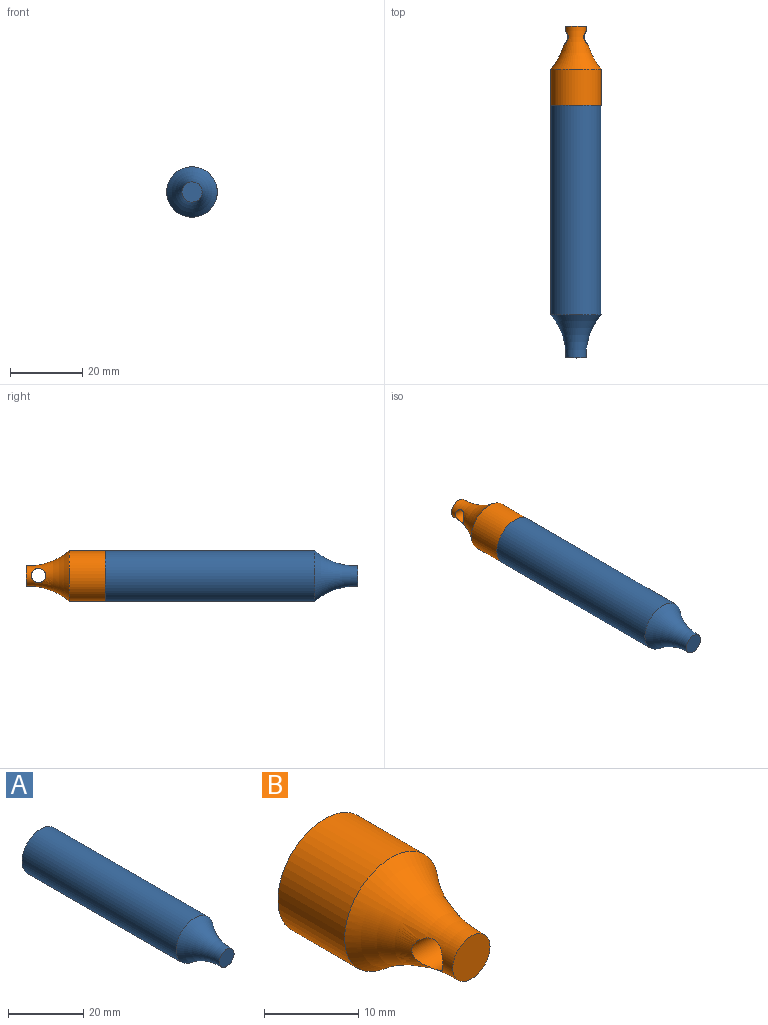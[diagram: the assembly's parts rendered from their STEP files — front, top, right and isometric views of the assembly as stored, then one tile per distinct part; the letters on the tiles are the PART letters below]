
ASSEMBLY  parts=2 mates=1
PART A: 6 faces, bbox 16.9x81.7x16.9 mm
  f0: plane 14x14mm, normal (0,1,0), area 21.2mm2, adj f1,f4
  f1: cylinder r=7mm len=58mm, axis (0,1,0), area 2551mm2, adj f0,f2
  f2: torus R=20.14mm, axis (0,1,0), area 338.6mm2, adj f1,f3
  f3: plane 5.58x5.58mm, normal (0,-1,0), area 24.5mm2, adj f2
  f4: cylinder r=6.5mm len=55.88mm, axis (0,1,0), area 2282.2mm2, adj f0,f5
  f5: plane 13x13mm, normal (0,1,0), area 132.7mm2, adj f4
PART B: 7 faces, bbox 16.9x33.7x16.9 mm
  f0: torus R=20.14mm, axis (0,-1,0), area 311.3mm2, adj f2,f3,f4
  f1: plane 14x14mm, normal (0,1,0), area 21.2mm2, adj f2,f5
  f2: cylinder r=7mm len=14mm, axis (0,-1,0), area 439.8mm2, adj f0,f1
  f3: plane 5.58x5.58mm, normal (0,-1,0), area 24.5mm2, adj f0
  f4: cylinder r=2mm len=6.92mm, axis (-1,0,0), area 67.9mm2, adj f0
  f5: cylinder r=6.5mm len=13mm, axis (0,1,0), area 367.6mm2, adj f1,f6
  f6: plane 13x13mm, normal (0,1,0), area 132.7mm2, adj f5
PLACE A t=(-33.3,13.91,-23.86)mm
PLACE B rot(axis=(1,0,0),180deg) t=(-33.3,-54.09,-23.86)mm
MATE fastened B.f5 <-> A.f1  axis (0,-1,0) through (-26.3,3.91,-23.86)mm
